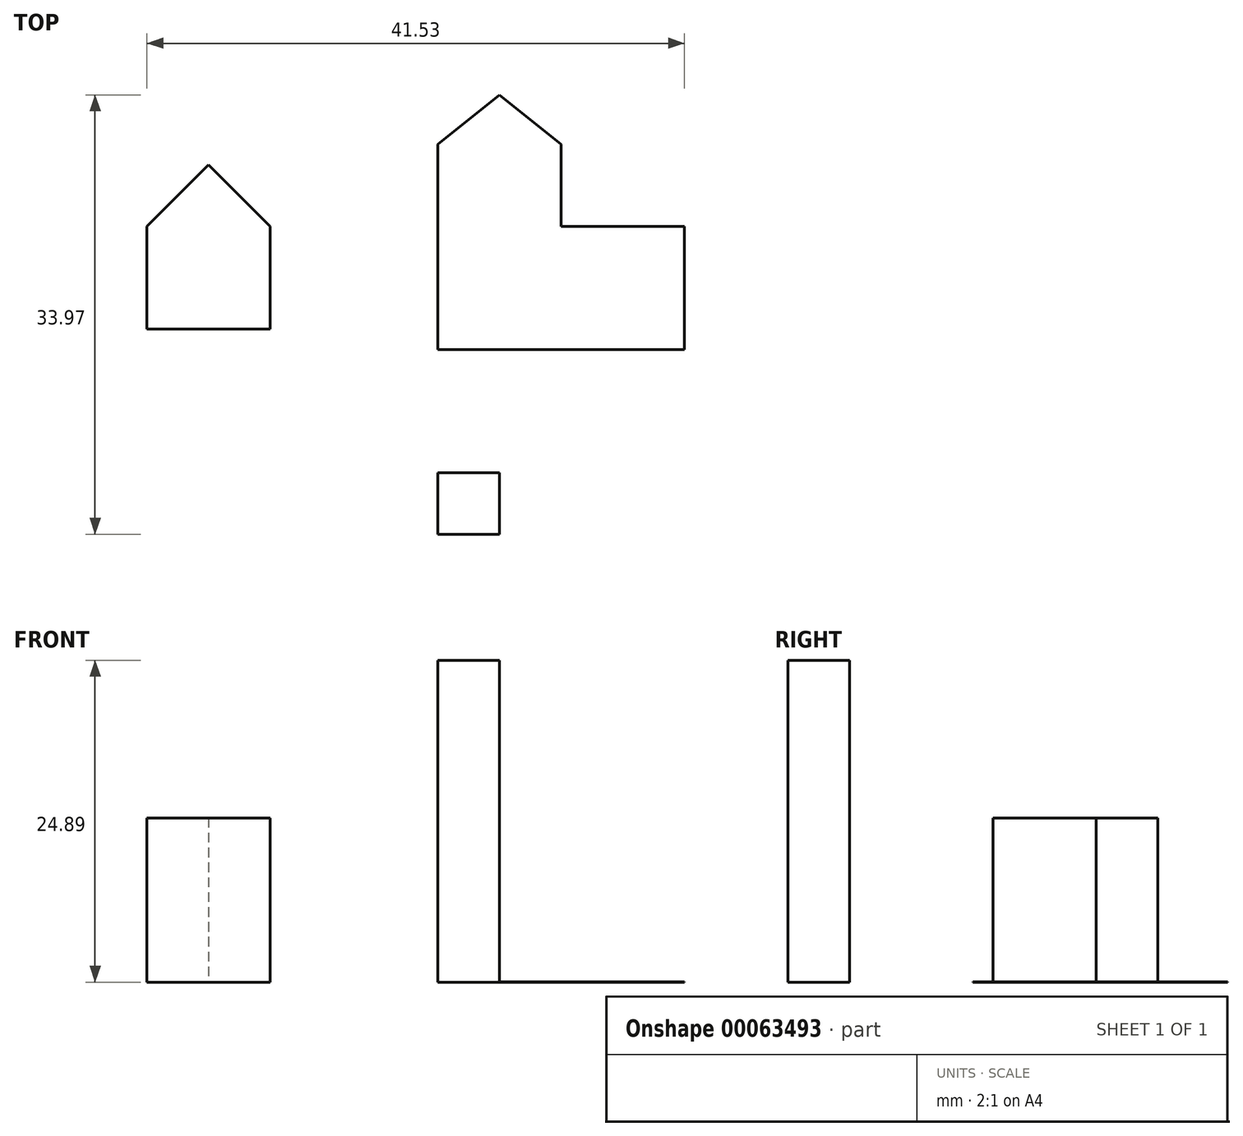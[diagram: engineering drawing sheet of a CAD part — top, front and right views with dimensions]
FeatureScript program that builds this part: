
annotation { "Feature Type Name" : "Feature", "Feature Type Description" : "" }
export const myFeature = defineFeature(function(context is Context, id is Id, definition is map)
    precondition{}
    {
        {
            var Q0;
            Q0=qCreatedBy(makeId("Top.planeOp"),FACE);
            var sketch = newSketch(context, id + "F0", { "sketchPlane" : qUnion([Q0])});
            skLineSegment(sketch, "E0.bottom", {"start": v(19.05, 0) * mm, "end": v(9.52, 0) * mm});
            skLineSegment(sketch, "E0.top", {"start": v(19.05, -9.53) * mm, "end": v(0, -9.53) * mm});
            skLineSegment(sketch, "E0.left", {"start": v(19.05, 0) * mm, "end": v(19.05, -9.53) * mm});
            skLineSegment(sketch, "E0.right", {"start": v(0, 0) * mm, "end": v(0, -9.53) * mm});
            skLineSegment(sketch, "E1.left", {"start": v(0, 0) * mm, "end": v(0, 6.35) * mm});
            skLineSegment(sketch, "E1.right", {"start": v(9.52, 0) * mm, "end": v(9.52, 6.35) * mm});
            skPoint(sketch, "E2.endSnap0", {"position": v(4.76, 6.35) * mm});
            skLineSegment(sketch, "E3", {"start": v(4.76, 10.16) * mm, "end": v(0, 6.35) * mm});
            skLineSegment(sketch, "E4", {"start": v(0, 6.35) * mm, "end": v(4.76, 10.16) * mm});
            skLineSegment(sketch, "E5", {"start": v(4.76, 10.16) * mm, "end": v(9.52, 6.35) * mm});
            skPoint(sketch, "E2.start.orphan", {"position": v(4.76, 6.35) * mm});
            skSolve(sketch);
        }
        {
            var Q0;
            Q0=makeQuery(id+"F0.imprint","IMPRINT",FACE,{"disambiguationData":[TD([[makeQuery(id+"F0.imprint","IMPRINT",EDGE,{"derivedFrom":sQuery(id+"F0.wireOp",EDGE,"E0.bottom")}),1.0]])]});
            extrude(context, id + "F1", {"entities" : qUnion([Q0]), "depth" : 3 / 203.2 * mm});
        }
        {
            var Q0;
            Q0=qCreatedBy(makeId("Top.planeOp"),FACE);
            var sketch = newSketch(context, id + "F2", { "sketchPlane" : qUnion([Q0])});
            skLineSegment(sketch, "E6.top", {"start": v(-22.48, -7.96) * mm, "end": v(-12.96, -7.96) * mm});
            skLineSegment(sketch, "E6.left", {"start": v(-22.48, 0) * mm, "end": v(-22.48, -7.96) * mm});
            skLineSegment(sketch, "E6.right", {"start": v(-12.96, 0) * mm, "end": v(-12.96, -7.96) * mm});
            skPoint(sketch, "E7.endSnap0", {"position": v(-17.72, 0) * mm});
            skLineSegment(sketch, "E8", {"start": v(-22.48, 0) * mm, "end": v(-17.72, 4.76) * mm});
            skLineSegment(sketch, "E9", {"start": v(-12.96, 0) * mm, "end": v(-17.72, 4.76) * mm});
            skPoint(sketch, "E7.start.orphan", {"position": v(-17.72, 0) * mm});
            skSolve(sketch);
        }
        {
            var Q0;
            Q0=makeQuery(id+"F2.imprint","IMPRINT",FACE,{"disambiguationData":[TD([[makeQuery(id+"F2.imprint","IMPRINT",EDGE,{"derivedFrom":sQuery(id+"F2.wireOp",EDGE,"E6.top")}),1.0]])]});
            extrude(context, id + "F3", {"entities" : qUnion([Q0]), "depth" : 12.7 * mm});
        }
        {
            var Q0;
            Q0=qCreatedBy(makeId("Top.planeOp"),FACE);
            var sketch = newSketch(context, id + "F4", { "sketchPlane" : qUnion([Q0])});
            skLineSegment(sketch, "E10.bottom", {"start": v(0, -19.05) * mm, "end": v(4.76, -19.05) * mm});
            skLineSegment(sketch, "E10.top", {"start": v(0, -23.81) * mm, "end": v(4.76, -23.81) * mm});
            skLineSegment(sketch, "E10.left", {"start": v(0, -19.05) * mm, "end": v(0, -23.81) * mm});
            skLineSegment(sketch, "E10.right", {"start": v(4.76, -19.05) * mm, "end": v(4.76, -23.81) * mm});
            skSolve(sketch);
        }
        {
            var Q0;
            Q0=makeQuery(id+"F4.imprint","IMPRINT",FACE,{"disambiguationData":[TD([[makeQuery(id+"F4.imprint","IMPRINT",EDGE,{"derivedFrom":sQuery(id+"F4.wireOp",EDGE,"E10.bottom")}),-1.0]])]});
            extrude(context, id + "F5", {"entities" : qUnion([Q0]), "depth" : 24.9 * mm});
        }
    });
